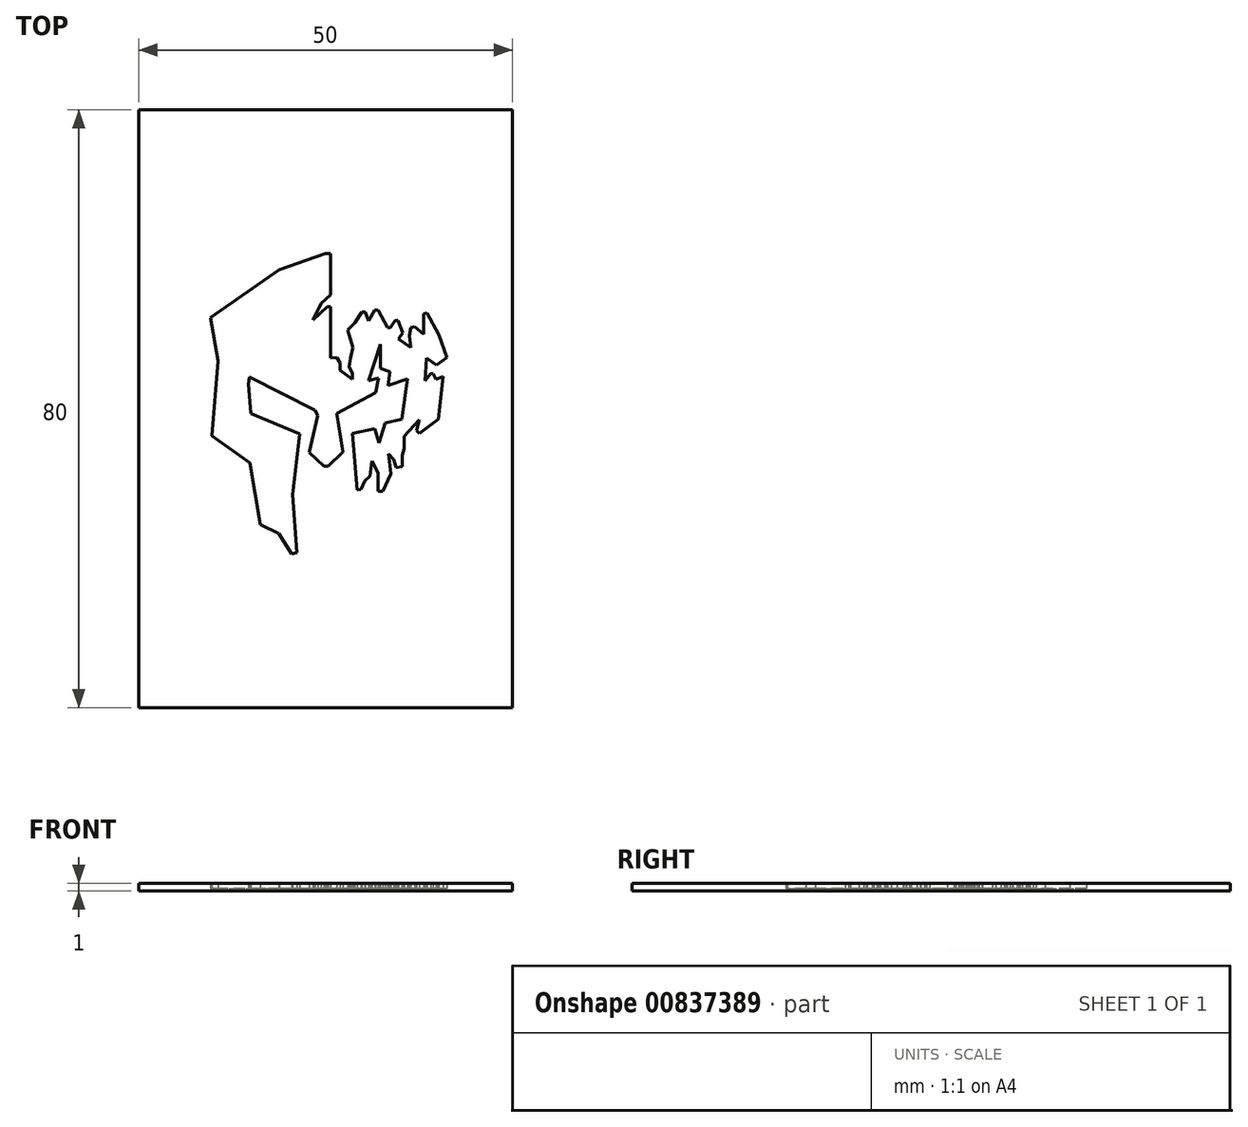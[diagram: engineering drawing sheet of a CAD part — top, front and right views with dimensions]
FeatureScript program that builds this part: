
annotation { "Feature Type Name" : "Feature", "Feature Type Description" : "" }
export const myFeature = defineFeature(function(context is Context, id is Id, definition is map)
    precondition{}
    {
        {
            var Q0;
            Q0=qCreatedBy(makeId("Top.planeOp"),FACE);
            var sketch = newSketch(context, id + "F0", { "sketchPlane" : qUnion([Q0])});
            skLineSegment(sketch, "E0", {"start": v(0.7, 20.78) * mm, "end": v(0, 20.78) * mm});
            skLineSegment(sketch, "E1", {"start": v(0, 20.78) * mm, "end": v(-6.16, 18.57) * mm});
            skLineSegment(sketch, "E2", {"start": v(-6.16, 18.57) * mm, "end": v(-15.4, 12.18) * mm});
            skLineSegment(sketch, "E3", {"start": v(-15.4, 12.18) * mm, "end": v(-14.38, 6.42) * mm});
            skLineSegment(sketch, "E4", {"start": v(-14.38, 6.42) * mm, "end": v(-15.2, -3.65) * mm});
            skLineSegment(sketch, "E5", {"start": v(-15.2, -3.65) * mm, "end": v(-10.12, -7.2) * mm});
            skLineSegment(sketch, "E6", {"start": v(-10.12, -7.2) * mm, "end": v(-8.75, -15.5) * mm});
            skLineSegment(sketch, "E7", {"start": v(-8.75, -15.5) * mm, "end": v(-6.25, -16.72) * mm});
            skLineSegment(sketch, "E8", {"start": v(-6.25, -16.72) * mm, "end": v(-4.5, -19.43) * mm});
            skLineSegment(sketch, "E9", {"start": v(-4.5, -19.43) * mm, "end": v(-3.8, -19.22) * mm});
            skLineSegment(sketch, "E10", {"start": v(-3.8, -19.22) * mm, "end": v(-4.4, -11.49) * mm});
            skLineSegment(sketch, "E11", {"start": v(-4.4, -11.49) * mm, "end": v(-3.44, -3.36) * mm});
            skLineSegment(sketch, "E12", {"start": v(-3.44, -3.36) * mm, "end": v(-9.96, -0.65) * mm});
            skLineSegment(sketch, "E13", {"start": v(-9.96, -0.65) * mm, "end": v(-10.32, 3.32) * mm});
            skLineSegment(sketch, "E14", {"start": v(-10.32, 3.32) * mm, "end": v(-10.17, 4.24) * mm});
            skLineSegment(sketch, "E15", {"start": v(-10.17, 4.24) * mm, "end": v(-1.4, -0.2) * mm});
            skLineSegment(sketch, "E16", {"start": v(-1.4, -0.2) * mm, "end": v(-1.04, -0.88) * mm});
            skLineSegment(sketch, "E17", {"start": v(-1.04, -0.88) * mm, "end": v(-2.2, -5.82) * mm});
            skLineSegment(sketch, "E18", {"start": v(-2.2, -5.82) * mm, "end": v(-0.24, -7.66) * mm});
            skLineSegment(sketch, "E19", {"start": v(-0.24, -7.66) * mm, "end": v(0.4, -7.66) * mm});
            skLineSegment(sketch, "E20", {"start": v(0.4, -7.66) * mm, "end": v(2.31, -5.8) * mm});
            skLineSegment(sketch, "E21", {"start": v(2.31, -5.8) * mm, "end": v(1.5, -0.65) * mm});
            skLineSegment(sketch, "E22", {"start": v(1.5, -0.65) * mm, "end": v(6.7, 2.17) * mm});
            skLineSegment(sketch, "E23", {"start": v(6.7, 2.17) * mm, "end": v(7.07, 4.13) * mm});
            skLineSegment(sketch, "E24", {"start": v(7.07, 4.13) * mm, "end": v(5.79, 3.72) * mm});
            skLineSegment(sketch, "E25", {"start": v(5.79, 3.72) * mm, "end": v(7.36, 8.64) * mm});
            skLineSegment(sketch, "E26", {"start": v(7.36, 8.64) * mm, "end": v(7.36, 5.37) * mm});
            skLineSegment(sketch, "E27", {"start": v(7.36, 5.37) * mm, "end": v(8.62, 4.95) * mm});
            skLineSegment(sketch, "E28", {"start": v(8.62, 4.95) * mm, "end": v(8.36, 3.09) * mm});
            skLineSegment(sketch, "E29", {"start": v(8.36, 3.09) * mm, "end": v(11, 4.02) * mm});
            skPoint(sketch, "E29.endSnap0", {"position": v(8.49, 4.02) * mm});
            skLineSegment(sketch, "E30", {"start": v(11, 4.02) * mm, "end": v(10.23, -1.37) * mm});
            skLineSegment(sketch, "E31", {"start": v(10.23, -1.37) * mm, "end": v(8.02, -1.9) * mm});
            skLineSegment(sketch, "E32", {"start": v(8.02, -1.9) * mm, "end": v(7.14, -4.58) * mm});
            skLineSegment(sketch, "E33", {"start": v(7.14, -4.58) * mm, "end": v(6.59, -2.66) * mm});
            skLineSegment(sketch, "E34", {"start": v(6.59, -2.66) * mm, "end": v(3.58, -3.3) * mm});
            skLineSegment(sketch, "E35", {"start": v(3.58, -3.3) * mm, "end": v(4.23, -10.86) * mm});
            skLineSegment(sketch, "E36", {"start": v(4.23, -10.86) * mm, "end": v(4.77, -10.81) * mm});
            skLineSegment(sketch, "E37", {"start": v(4.77, -10.81) * mm, "end": v(5.25, -9.65) * mm});
            skLineSegment(sketch, "E38", {"start": v(5.25, -9.65) * mm, "end": v(5.93, -9) * mm});
            skLineSegment(sketch, "E39", {"start": v(5.93, -9) * mm, "end": v(6.2, -7) * mm});
            skLineSegment(sketch, "E40", {"start": v(6.2, -7) * mm, "end": v(7.06, -8.59) * mm});
            skLineSegment(sketch, "E41", {"start": v(7.06, -8.59) * mm, "end": v(7.06, -11.03) * mm});
            skLineSegment(sketch, "E42", {"start": v(7.06, -11.03) * mm, "end": v(7.65, -11.03) * mm});
            skLineSegment(sketch, "E43", {"start": v(7.65, -11.03) * mm, "end": v(8.74, -8.68) * mm});
            skLineSegment(sketch, "E44", {"start": v(8.74, -8.68) * mm, "end": v(8.42, -6.06) * mm});
            skLineSegment(sketch, "E45", {"start": v(8.42, -6.06) * mm, "end": v(9.11, -6.79) * mm});
            skLineSegment(sketch, "E46", {"start": v(9.11, -6.79) * mm, "end": v(9.44, -7.87) * mm});
            skLineSegment(sketch, "E47", {"start": v(9.44, -7.87) * mm, "end": v(10.25, -7.72) * mm});
            skLineSegment(sketch, "E48", {"start": v(10.25, -7.72) * mm, "end": v(10.25, -6.2) * mm});
            skLineSegment(sketch, "E49", {"start": v(10.25, -6.2) * mm, "end": v(10.54, -5.33) * mm});
            skLineSegment(sketch, "E50", {"start": v(10.54, -5.33) * mm, "end": v(10.54, -3.71) * mm});
            skLineSegment(sketch, "E51", {"start": v(10.54, -3.71) * mm, "end": v(12.53, -1.48) * mm});
            skLineSegment(sketch, "E52", {"start": v(12.53, -1.48) * mm, "end": v(12.18, -2.93) * mm});
            skLineSegment(sketch, "E53", {"start": v(12.18, -2.93) * mm, "end": v(12.57, -3.3) * mm});
            skLineSegment(sketch, "E54", {"start": v(12.57, -3.3) * mm, "end": v(15.1, -1.42) * mm});
            skLineSegment(sketch, "E55", {"start": v(15.1, -1.42) * mm, "end": v(15.74, 4.33) * mm});
            skLineSegment(sketch, "E56", {"start": v(15.74, 4.33) * mm, "end": v(14.8, 3.97) * mm});
            skLineSegment(sketch, "E57", {"start": v(14.8, 3.97) * mm, "end": v(14.42, 4.67) * mm});
            skLineSegment(sketch, "E58", {"start": v(14.42, 4.67) * mm, "end": v(14.07, 4.67) * mm});
            skLineSegment(sketch, "E59", {"start": v(14.07, 4.67) * mm, "end": v(13.33, 3.73) * mm});
            skLineSegment(sketch, "E60", {"start": v(13.33, 3.73) * mm, "end": v(13.48, 6.81) * mm});
            skLineSegment(sketch, "E61", {"start": v(13.48, 6.81) * mm, "end": v(14.83, 5.87) * mm});
            skLineSegment(sketch, "E62", {"start": v(14.83, 5.87) * mm, "end": v(16.22, 6.84) * mm});
            skLineSegment(sketch, "E63", {"start": v(16.22, 6.84) * mm, "end": v(15.17, 9.89) * mm});
            skLineSegment(sketch, "E64", {"start": v(15.17, 9.89) * mm, "end": v(13.58, 12.83) * mm});
            skLineSegment(sketch, "E65", {"start": v(13.58, 12.83) * mm, "end": v(13.13, 12.7) * mm});
            skLineSegment(sketch, "E66", {"start": v(13.13, 12.7) * mm, "end": v(13.13, 10) * mm});
            skLineSegment(sketch, "E67", {"start": v(13.13, 10) * mm, "end": v(11.92, 10.96) * mm});
            skLineSegment(sketch, "E68", {"start": v(11.92, 10.96) * mm, "end": v(11.44, 10.87) * mm});
            skLineSegment(sketch, "E69", {"start": v(11.44, 10.87) * mm, "end": v(11.25, 9.76) * mm});
            skLineSegment(sketch, "E70", {"start": v(11.25, 9.76) * mm, "end": v(11.44, 8.17) * mm});
            skLineSegment(sketch, "E71", {"start": v(11.44, 8.17) * mm, "end": v(9.74, 9.32) * mm});
            skLineSegment(sketch, "E72", {"start": v(9.74, 9.32) * mm, "end": v(10.33, 10.2) * mm});
            skLineSegment(sketch, "E73", {"start": v(10.33, 10.2) * mm, "end": v(9.71, 11.83) * mm});
            skLineSegment(sketch, "E74", {"start": v(9.71, 11.83) * mm, "end": v(9.29, 11.83) * mm});
            skLineSegment(sketch, "E75", {"start": v(9.29, 11.83) * mm, "end": v(8.7, 10.87) * mm});
            skLineSegment(sketch, "E76", {"start": v(8.7, 10.87) * mm, "end": v(8.27, 10.87) * mm});
            skLineSegment(sketch, "E77", {"start": v(8.27, 10.87) * mm, "end": v(7.01, 13.2) * mm});
            skLineSegment(sketch, "E78", {"start": v(7.01, 13.2) * mm, "end": v(6.59, 13.2) * mm});
            skLineSegment(sketch, "E79", {"start": v(6.59, 13.2) * mm, "end": v(5.75, 11.72) * mm});
            skLineSegment(sketch, "E80", {"start": v(5.75, 11.72) * mm, "end": v(5.34, 12.98) * mm});
            skLineSegment(sketch, "E81", {"start": v(5.34, 12.98) * mm, "end": v(4.88, 12.97) * mm});
            skLineSegment(sketch, "E82", {"start": v(4.88, 12.97) * mm, "end": v(3.91, 11.52) * mm});
            skLineSegment(sketch, "E83", {"start": v(3.91, 11.52) * mm, "end": v(2.97, 10.52) * mm});
            skLineSegment(sketch, "E84", {"start": v(2.97, 10.52) * mm, "end": v(3.67, 8.18) * mm});
            skLineSegment(sketch, "E85", {"start": v(3.67, 8.18) * mm, "end": v(3.34, 6.8) * mm});
            skLineSegment(sketch, "E86", {"start": v(3.34, 6.8) * mm, "end": v(3.18, 5.59) * mm});
            skLineSegment(sketch, "E87", {"start": v(3.18, 5.59) * mm, "end": v(3.58, 4.74) * mm});
            skLineSegment(sketch, "E88", {"start": v(3.58, 4.74) * mm, "end": v(3.63, 3.92) * mm});
            skLineSegment(sketch, "E89", {"start": v(3.63, 3.92) * mm, "end": v(1.95, 5.15) * mm});
            skLineSegment(sketch, "E90", {"start": v(1.95, 5.15) * mm, "end": v(1.95, 6.18) * mm});
            skLineSegment(sketch, "E91", {"start": v(1.95, 6.18) * mm, "end": v(1.5, 6.89) * mm});
            skLineSegment(sketch, "E92", {"start": v(1.5, 6.89) * mm, "end": v(0.68, 6.8) * mm});
            skLineSegment(sketch, "E93", {"start": v(0.68, 6.8) * mm, "end": v(0.68, 13.65) * mm});
            skLineSegment(sketch, "E94", {"start": v(0.68, 13.65) * mm, "end": v(0.22, 13.65) * mm});
            skLineSegment(sketch, "E95", {"start": v(0.22, 13.65) * mm, "end": v(-1.67, 11.85) * mm});
            skLineSegment(sketch, "E96", {"start": v(-1.67, 11.85) * mm, "end": v(-0.58, 14.07) * mm});
            skLineSegment(sketch, "E97", {"start": v(-0.58, 14.07) * mm, "end": v(0.71, 15.27) * mm});
            skLineSegment(sketch, "E98", {"start": v(0.71, 15.27) * mm, "end": v(0.7, 20.78) * mm});
            skLineSegment(sketch, "E99", {"start": v(15.74, 4.33) * mm, "end": v(15.1, -1.42) * mm});
            skLineSegment(sketch, "E100", {"start": v(13.48, 6.81) * mm, "end": v(13.33, 3.73) * mm});
            skSolve(sketch);
        }
        {
            var Q0;
            Q0=makeQuery(id+"F0.imprint","IMPRINT",FACE,{"disambiguationData":[TD([[makeQuery(id+"F0.imprint","IMPRINT",EDGE,{"derivedFrom":sQuery(id+"F0.wireOp",EDGE,"E0")}),1.0]])]});
            var Q1;
            Q1=makeQuery(id+"F0.imprint","IMPRINT",FACE,{"disambiguationData":[TD([[makeQuery(id+"F0.imprint","IMPRINT",EDGE,{"derivedFrom":sQuery(id+"F0.wireOp",EDGE,"E4")}),-1.0]])]});
            var Q2;
            Q2=makeQuery(id+"F0.imprint","IMPRINT",FACE,{"disambiguationData":[TD([[makeQuery(id+"F0.imprint","IMPRINT",EDGE,{"derivedFrom":sQuery(id+"F0.wireOp",EDGE,"E54")}),-1.0]])]});
            extrude(context, id + "F1", {"entities" : qUnion([Q0, Q1, Q2]), "depth" : 0.3 * mm, "offsetDistance" : 25 * mm});
        }
        {
            var Q0;
            Q0=makeQuery(id+"F1.opExtrude","CAP_FACE",FACE,{"disambiguationData":[OSD([sQuery(id+"F0.wireOp",EDGE,"E0"),sQuery(id+"F0.wireOp",EDGE,"E1"),sQuery(id+"F0.wireOp",EDGE,"E2"),sQuery(id+"F0.wireOp",EDGE,"E3"),sQuery(id+"F0.wireOp",EDGE,"E4"),sQuery(id+"F0.wireOp",EDGE,"E5"),sQuery(id+"F0.wireOp",EDGE,"E6"),sQuery(id+"F0.wireOp",EDGE,"E7"),sQuery(id+"F0.wireOp",EDGE,"E8"),sQuery(id+"F0.wireOp",EDGE,"E9"),sQuery(id+"F0.wireOp",EDGE,"E10"),sQuery(id+"F0.wireOp",EDGE,"E11"),sQuery(id+"F0.wireOp",EDGE,"E12"),sQuery(id+"F0.wireOp",EDGE,"E13"),sQuery(id+"F0.wireOp",EDGE,"E14"),sQuery(id+"F0.wireOp",EDGE,"E15"),sQuery(id+"F0.wireOp",EDGE,"E16"),sQuery(id+"F0.wireOp",EDGE,"E17"),sQuery(id+"F0.wireOp",EDGE,"E18"),sQuery(id+"F0.wireOp",EDGE,"E19"),sQuery(id+"F0.wireOp",EDGE,"E20"),sQuery(id+"F0.wireOp",EDGE,"E21"),sQuery(id+"F0.wireOp",EDGE,"E22"),sQuery(id+"F0.wireOp",EDGE,"E23"),sQuery(id+"F0.wireOp",EDGE,"E24"),sQuery(id+"F0.wireOp",EDGE,"E25"),sQuery(id+"F0.wireOp",EDGE,"E26"),sQuery(id+"F0.wireOp",EDGE,"E27"),sQuery(id+"F0.wireOp",EDGE,"E28"),sQuery(id+"F0.wireOp",EDGE,"E29"),sQuery(id+"F0.wireOp",EDGE,"E30"),sQuery(id+"F0.wireOp",EDGE,"E31"),sQuery(id+"F0.wireOp",EDGE,"E32"),sQuery(id+"F0.wireOp",EDGE,"E33"),sQuery(id+"F0.wireOp",EDGE,"E34"),sQuery(id+"F0.wireOp",EDGE,"E35"),sQuery(id+"F0.wireOp",EDGE,"E36"),sQuery(id+"F0.wireOp",EDGE,"E37"),sQuery(id+"F0.wireOp",EDGE,"E38"),sQuery(id+"F0.wireOp",EDGE,"E39"),sQuery(id+"F0.wireOp",EDGE,"E40"),sQuery(id+"F0.wireOp",EDGE,"E41"),sQuery(id+"F0.wireOp",EDGE,"E42"),sQuery(id+"F0.wireOp",EDGE,"E43"),sQuery(id+"F0.wireOp",EDGE,"E44"),sQuery(id+"F0.wireOp",EDGE,"E45"),sQuery(id+"F0.wireOp",EDGE,"E46"),sQuery(id+"F0.wireOp",EDGE,"E47"),sQuery(id+"F0.wireOp",EDGE,"E48"),sQuery(id+"F0.wireOp",EDGE,"E49"),sQuery(id+"F0.wireOp",EDGE,"E50"),sQuery(id+"F0.wireOp",EDGE,"E51"),sQuery(id+"F0.wireOp",EDGE,"E52"),sQuery(id+"F0.wireOp",EDGE,"E53"),sQuery(id+"F0.wireOp",EDGE,"E54"),sQuery(id+"F0.wireOp",EDGE,"E56"),sQuery(id+"F0.wireOp",EDGE,"E57"),sQuery(id+"F0.wireOp",EDGE,"E58"),sQuery(id+"F0.wireOp",EDGE,"E59"),sQuery(id+"F0.wireOp",EDGE,"E61"),sQuery(id+"F0.wireOp",EDGE,"E62"),sQuery(id+"F0.wireOp",EDGE,"E63"),sQuery(id+"F0.wireOp",EDGE,"E64"),sQuery(id+"F0.wireOp",EDGE,"E65"),sQuery(id+"F0.wireOp",EDGE,"E66"),sQuery(id+"F0.wireOp",EDGE,"E67"),sQuery(id+"F0.wireOp",EDGE,"E68"),sQuery(id+"F0.wireOp",EDGE,"E69"),sQuery(id+"F0.wireOp",EDGE,"E70"),sQuery(id+"F0.wireOp",EDGE,"E71"),sQuery(id+"F0.wireOp",EDGE,"E72"),sQuery(id+"F0.wireOp",EDGE,"E73"),sQuery(id+"F0.wireOp",EDGE,"E74"),sQuery(id+"F0.wireOp",EDGE,"E75"),sQuery(id+"F0.wireOp",EDGE,"E76"),sQuery(id+"F0.wireOp",EDGE,"E77"),sQuery(id+"F0.wireOp",EDGE,"E78"),sQuery(id+"F0.wireOp",EDGE,"E79"),sQuery(id+"F0.wireOp",EDGE,"E80"),sQuery(id+"F0.wireOp",EDGE,"E81"),sQuery(id+"F0.wireOp",EDGE,"E82"),sQuery(id+"F0.wireOp",EDGE,"E83"),sQuery(id+"F0.wireOp",EDGE,"E84"),sQuery(id+"F0.wireOp",EDGE,"E85"),sQuery(id+"F0.wireOp",EDGE,"E86"),sQuery(id+"F0.wireOp",EDGE,"E87"),sQuery(id+"F0.wireOp",EDGE,"E88"),sQuery(id+"F0.wireOp",EDGE,"E89"),sQuery(id+"F0.wireOp",EDGE,"E90"),sQuery(id+"F0.wireOp",EDGE,"E91"),sQuery(id+"F0.wireOp",EDGE,"E92"),sQuery(id+"F0.wireOp",EDGE,"E93"),sQuery(id+"F0.wireOp",EDGE,"E94"),sQuery(id+"F0.wireOp",EDGE,"E95"),sQuery(id+"F0.wireOp",EDGE,"E96"),sQuery(id+"F0.wireOp",EDGE,"E97"),sQuery(id+"F0.wireOp",EDGE,"E98"),sQuery(id+"F0.wireOp",EDGE,"E100"),sQuery(id+"F0.wireOp",EDGE,"E99")])],"isStart":true});
            var sketch = newSketch(context, id + "F2", { "sketchPlane" : qUnion([Q0])});
            skLineSegment(sketch, "E101.bottom", {"start": v(-25, 40) * mm, "end": v(25, 40) * mm});
            skLineSegment(sketch, "E101.top", {"start": v(-25, -40) * mm, "end": v(25, -40) * mm});
            skLineSegment(sketch, "E101.left", {"start": v(-25, 40) * mm, "end": v(-25, -40) * mm});
            skLineSegment(sketch, "E101.right", {"start": v(25, 40) * mm, "end": v(25, -40) * mm});
            skSolve(sketch);
        }
        {
            var Q0;
            Q0=makeQuery(id+"F2.imprint","IMPRINT",FACE,{"disambiguationData":[TD([[makeQuery(id+"F2.imprint","IMPRINT",EDGE,{"derivedFrom":sQuery(id+"F2.wireOp",EDGE,"E101.bottom")}),-1.0]])]});
            extrude(context, id + "F3", {"entities" : qUnion([Q0]), "operationType" : NewBodyOperationType.ADD, "oppositeDirection" : true, "depth" : 1 * mm, "offsetDistance" : 25 * mm});
        }
    });
